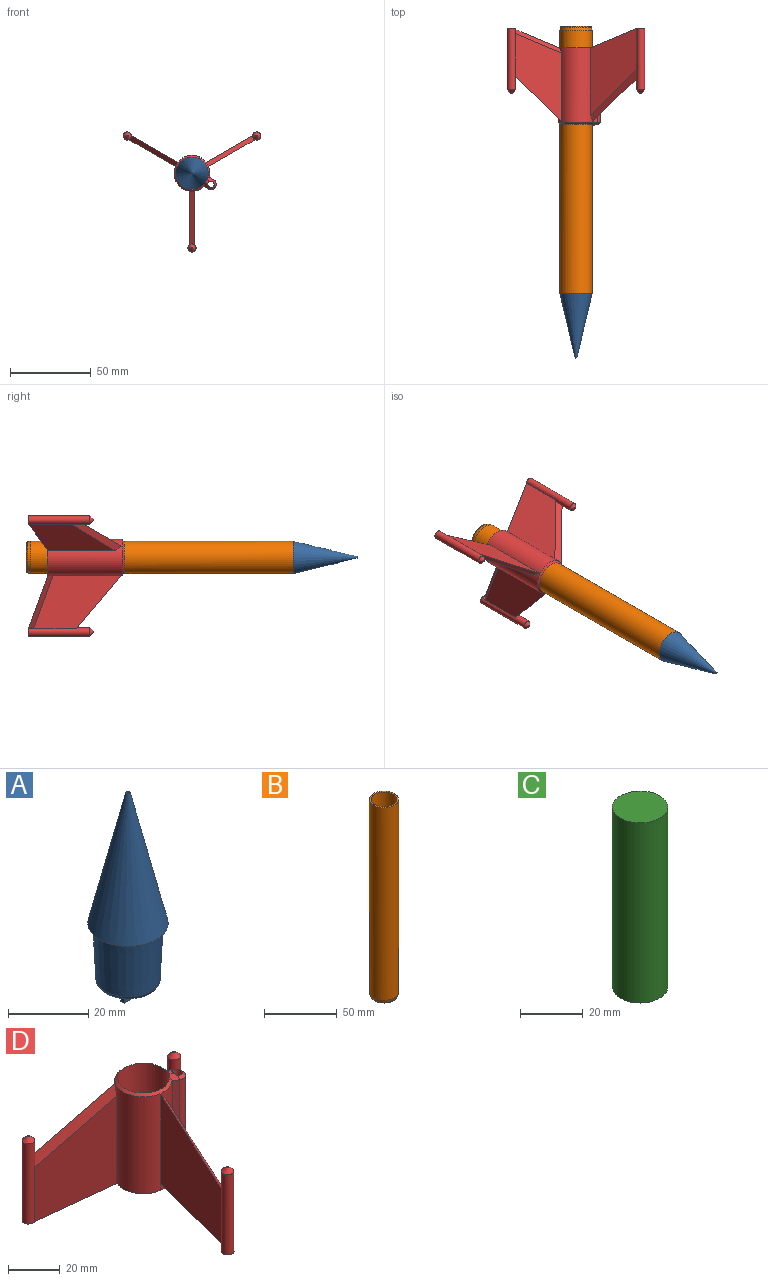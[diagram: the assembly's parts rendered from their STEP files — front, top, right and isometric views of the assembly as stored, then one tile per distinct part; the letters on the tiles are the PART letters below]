
ASSEMBLY  parts=4 mates=3
PART A: 15 faces, bbox 20x20x63 mm
  f0: plane 5x4mm, normal (0,-1,0), area 12mm2, adj f1,f8,f10,f11,f12,f13,f14
  f1: plane 13.42x13.42mm, normal (0,0,-1), area 139mm2, adj f0,f7,f8,f9,f10,f12,f14
  f2: plane 20x20mm, normal (0,0,-1), area 70.9mm2, adj f4,f6
  f3: plane 0.52x0.52mm, normal (0,0,1), area 0.2mm2, adj f5
  f4: cone r=10mm half-angle=13.4deg, axis (0,0,-1), area 1355.4mm2, adj f2,f5
  f5: torus R=0.26mm, axis (0,0,1), area 1.1mm2, adj f3,f4
  f6: cone r=8.8mm half-angle=2.7deg, axis (0,0,1), area 886.1mm2, adj f2,f7
  f7: torus R=6.71mm, axis (0,0,-1), area 93.6mm2, adj f1,f6
  f8: plane 5x1.2mm, normal (-1,0,0), area 6mm2, adj f0,f1,f9,f11
  f9: plane 5x4mm, normal (0,1,0), area 12mm2, adj f1,f8,f10,f11,f12,f13,f14
  f10: plane 5x1.2mm, normal (1,0,0), area 6mm2, adj f0,f1,f9,f11
  f11: plane 4x1.2mm, normal (0,0,-1), area 4.8mm2, adj f0,f8,f9,f10
  f12: plane 4x1.2mm, normal (1,0,0), area 4.8mm2, adj f0,f1,f9,f13
  f13: plane 2x1.2mm, normal (0,0,1), area 2.4mm2, adj f0,f9,f12,f14
  f14: plane 4x1.2mm, normal (-1,0,0), area 4.8mm2, adj f0,f1,f9,f13
PART B: 10 faces, bbox 20x20x165 mm
  f0: cylinder r=8.8mm len=75mm, axis (0,0,1), area 4146.9mm2, adj f2,f6
  f1: cylinder r=10mm len=162mm, axis (0,0,1), area 10178.8mm2, adj f5,f9
  f2: plane 18x18mm, normal (0,0,-1), area 11.2mm2, adj f0,f3
  f3: cone r=10mm half-angle=45deg, axis (0,0,1), area 23.8mm2, adj f2,f4
  f4: cone r=10mm half-angle=22.5deg, axis (0,0,1), area 50.4mm2, adj f3,f5
  f5: cone r=10mm half-angle=11.3deg, axis (0,0,1), area 120.9mm2, adj f1,f4
  f6: plane 17.6x17.6mm, normal (0,0,-1), area 243.3mm2, adj f0
  f7: plane 17.6x17.6mm, normal (0,0,1), area 243.3mm2, adj f8
  f8: cylinder r=8.8mm len=81mm, axis (0,0,-1), area 4478.7mm2, adj f7,f9
  f9: plane 20x20mm, normal (0,0,1), area 70.9mm2, adj f1,f8
PART C: 3 faces, bbox 17.6x17.6x70 mm
  f0: cylinder r=8.8mm len=70mm, axis (0,0,-1), area 3870.4mm2, adj f1,f2
  f1: plane 17.6x17.6mm, normal (0,0,1), area 243.3mm2, adj f0
  f2: plane 17.6x17.6mm, normal (0,0,-1), area 243.3mm2, adj f0
PART D: 40 faces, bbox 85.2x74.5x60.4 mm
  f0: plane 3.24x2.6mm, normal (-0.87,0.5,0), area 4.9mm2, adj f23,f34,f35
  f1: plane 3.24x3mm, normal (0,-1,0), area 4.9mm2, adj f23,f32,f35
  f2: plane 3.24x2.6mm, normal (0.87,0.5,0), area 4.9mm2, adj f23,f33,f35
  f3: plane 33.1x31.69mm, normal (0.71,-0.45,0.54), area 181.1mm2, adj f8,f13,f14,f23
  f4: plane 31.69x30.17mm, normal (0.04,0.84,0.54), area 181.1mm2, adj f6,f18,f19,f23
  f5: plane 31.69x30.17mm, normal (-0.75,-0.39,0.54), area 181.1mm2, adj f11,f20,f21,f23
  f6: cylinder r=2.5mm len=38mm, axis (0,0,-1), area 512.1mm2, adj f4,f7,f18,f19,f30,f33
  f7: plane 5x5mm, normal (0,0,-1), area 19.6mm2, adj f6
  f8: cylinder r=2.5mm len=38mm, axis (0,0,-1), area 506.6mm2, adj f3,f9,f10,f13,f14,f31
  f9: cylinder r=2.5mm len=3.19mm, axis (0,0,-1), area 5.5mm2, adj f8,f10,f32
  f10: plane 5x5mm, normal (0,0,-1), area 19.6mm2, adj f8,f9
  f11: cylinder r=2.5mm len=38mm, axis (0,0,-1), area 512.1mm2, adj f5,f12,f20,f21,f29,f34
  f12: plane 5x5mm, normal (0,0,-1), area 19.6mm2, adj f11
  f13: plane 54.2x33.1mm, normal (-1,0,0), area 1134.9mm2, adj f3,f8,f23,f32
  f14: plane 53.47x33.1mm, normal (1,0,0), area 1111mm2, adj f3,f8,f23,f32
  f15: plane 46x2.52mm, normal (-0.5,-0.87,0), area 133.7mm2, adj f16,f23,f35,f39
  f16: cylinder r=3.25mm len=46mm, axis (0,0,-1), area 469.7mm2, adj f15,f17,f35,f37
  f17: plane 46x2.52mm, normal (0.5,0.87,0), area 133.7mm2, adj f16,f23,f35,f36
  f18: plane 54.2x28.67mm, normal (0.5,-0.87,0), area 1134.9mm2, adj f4,f6,f23,f33
  f19: plane 53.47x28.67mm, normal (-0.5,0.87,0), area 1111mm2, adj f4,f6,f23,f33
  f20: plane 54.2x28.67mm, normal (0.5,0.87,0), area 1134.9mm2, adj f5,f11,f23,f34
  f21: plane 53.47x28.67mm, normal (-0.5,-0.87,0), area 1111mm2, adj f5,f11,f23,f34
  f22: cylinder r=10mm len=48mm, axis (0,0,-1), area 2962.5mm2, adj f25,f35,f36,f38,f39
  f23: cylinder r=11.1mm len=46mm, axis (0,0,-1), area 2513.2mm2, adj f0,f1,f2,f3,f4,f5,f13,f14
  f24: cylinder r=2mm len=48mm, axis (0,0,-1), area 597.1mm2, adj f25,f35,f36,f37,f39
  f25: plane 3.18x3.01mm, normal (0,0,1), area 4.2mm2, adj f22,f24,f36,f39
  f26: plane 1x1mm, normal (0,0,1), area 0.8mm2, adj f29
  f27: plane 1x1mm, normal (0,0,1), area 0.8mm2, adj f31
  f28: plane 1x1mm, normal (0,0,1), area 0.8mm2, adj f30
  f29: cone r=0.5mm half-angle=45deg, axis (0,0,-1), area 26.6mm2, adj f11,f26
  f30: cone r=0.5mm half-angle=45deg, axis (0,0,-1), area 26.6mm2, adj f6,f28
  f31: cone r=0.5mm half-angle=45deg, axis (0,0,-1), area 26.6mm2, adj f8,f27
  f32: plane 33.1x15.24mm, normal (-0.71,0.24,-0.66), area 147.9mm2, adj f1,f9,f13,f14
  f33: plane 30.17x19.15mm, normal (0.14,-0.73,-0.66), area 147.9mm2, adj f2,f6,f18,f19
  f34: plane 30.17x19.15mm, normal (0.56,0.49,-0.66), area 147.9mm2, adj f0,f11,f20,f21
  f35: plane 26.06x22.1mm, normal (0,0,-1), area 93.1mm2, adj f0,f1,f2,f15,f16,f17,f22,f23
  f36: plane 4.47x2.89mm, normal (0.35,0.61,0.71), area 8.7mm2, adj f17,f22,f24,f25,f37,f38
  f37: cone r=1.25mm half-angle=45deg, axis (0,0,-1), area 14.6mm2, adj f16,f24,f36,f39
  f38: cone r=9.1mm half-angle=45deg, axis (0,0,-1), area 94.7mm2, adj f22,f23,f36,f39
  f39: plane 3.89x3.68mm, normal (-0.35,-0.61,0.71), area 8.7mm2, adj f15,f22,f24,f25,f37,f38
PLACE A rot(axis=(1,0,0),90deg) t=(0,-160,0)mm
PLACE B rot(axis=(1,0,0),90deg) t=(0,-70,0)mm
PLACE C rot(axis=(1,0,0),90deg) t=(0,0,0)mm
PLACE D rot(axis=(1,0,0),90deg) t=(0,3.5,0)mm
MATE fastened A.f4 <-> B.f1  axis (0,1,0) through (0,-160,0)mm
MATE fastened D.f22 <-> B.f0  axis (0,1,0) through (0,-32.5,0)mm
MATE fastened C.f0 <-> B.f0  axis (0,-1,0) through (0,-70,0)mm
